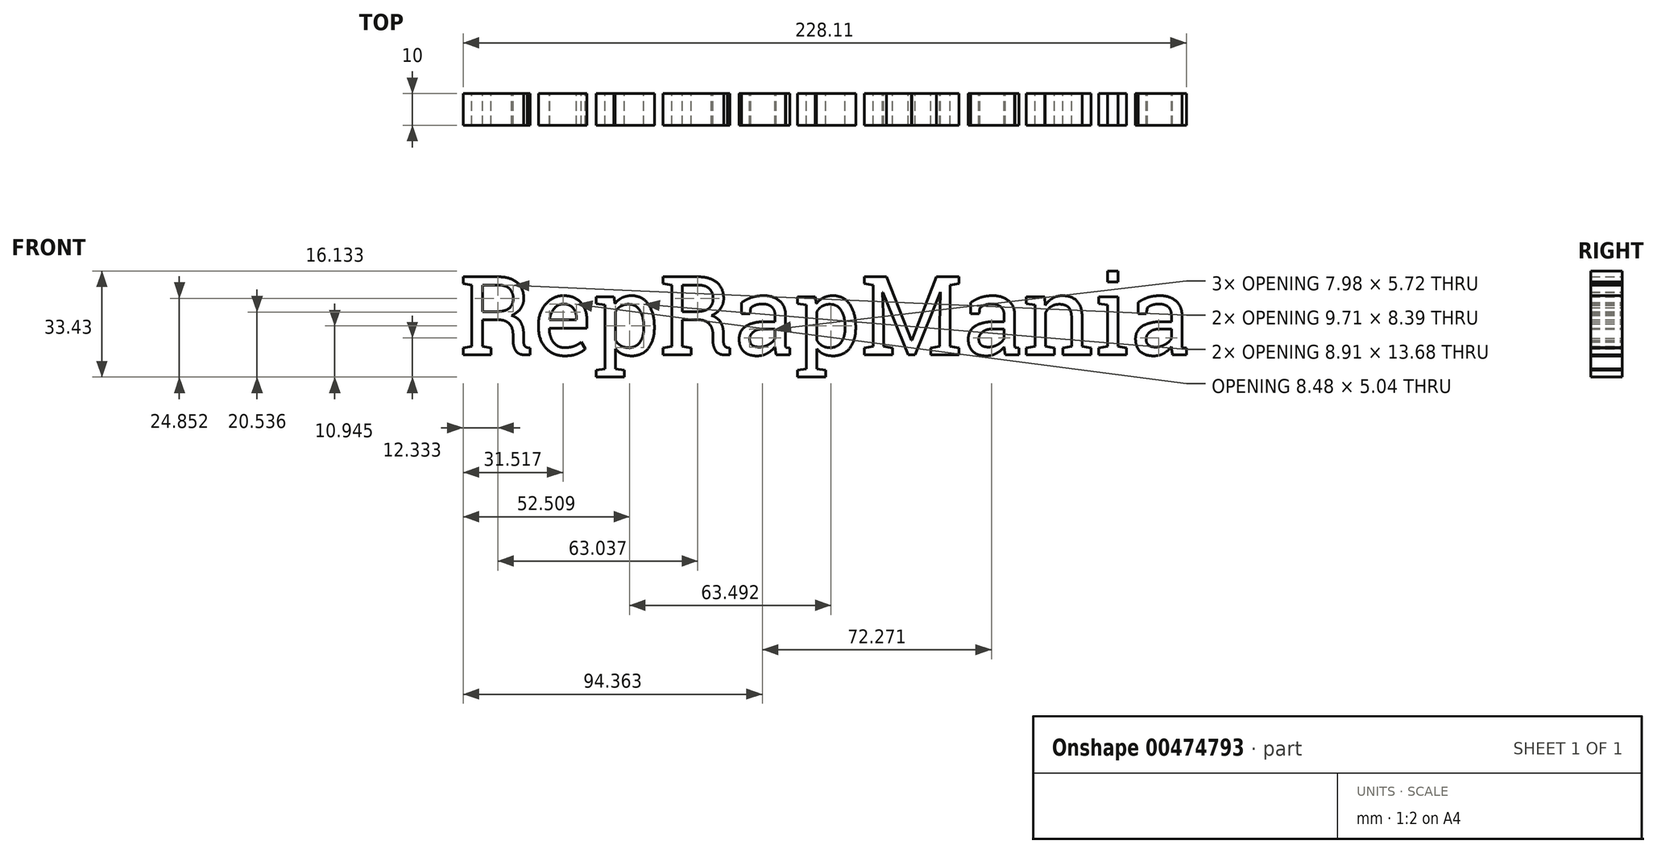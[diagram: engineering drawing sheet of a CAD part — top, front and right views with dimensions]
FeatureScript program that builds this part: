
annotation { "Feature Type Name" : "Feature", "Feature Type Description" : "" }
export const myFeature = defineFeature(function(context is Context, id is Id, definition is map)
    precondition{}
    {
        {
            var Q0;
            Q0=qCreatedBy(makeId("Front.planeOp"),FACE);
            var sketch = newSketch(context, id + "F0", { "sketchPlane" : qUnion([Q0])});
            skText(sketch, "E0", { "text": "RepRapMania", "fontName": "RobotoSlab-Regular.ttf"});
            const initialGuessF0  = {"E0": [-0.11573, 0, 1, 0, 0.02494]};
            skSetInitialGuess(sketch, initialGuessF0);
            skSolve(sketch);
        }
        {
            var Q0;
            Q0 = qSketchRegion(id + "F0", true);
            extrude(context, id + "F1", {"entities" : qUnion([Q0]), "depth" : 10 * mm});
        }
    });
